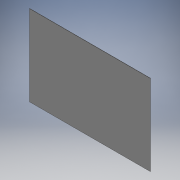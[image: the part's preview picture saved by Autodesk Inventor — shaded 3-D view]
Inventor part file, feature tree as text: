
AUTODESK INVENTOR PART (.ipt)
format: ipt  version: 2016 (Build 200138000, 138)  size: 96,256 bytes
history: native  units: mm
features: extrude x1, sketch x1
ambient origin geometry x8: Origin, YZ Plane, XZ Plane, XY Plane, X Axis, Y Axis, Z Axis, Center Point
bodies: Solid1 (feature_tree)
feature tree (2):
  extrude  "Extrusion1"  Depth=6000.0mm
  sketch  "Sketch1"  dims[d0=9000.0mm d1=6000.0mm d2=20.0mm d3=0.0mm]
